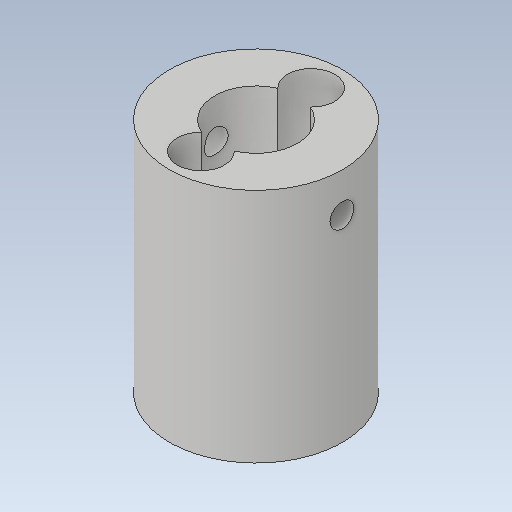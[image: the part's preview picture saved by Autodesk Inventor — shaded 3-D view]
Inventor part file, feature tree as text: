
AUTODESK INVENTOR PART (.ipt)
format: ipt  version: 2020.1 (Build 241239000, 239)  size: 161,792 bytes
history: native  units: mm
features: extrude x5, sketch x5, other x2
ambient origin geometry x8: Origin, YZ Plane, XZ Plane, XY Plane, X Axis, Y Axis, Z Axis, Center Point
bodies: Body1 (feature_tree)
feature tree (12):
  extrude  "Extrusión6"  Depth=7.0mm
  extrude  "Extrusión7"  Depth=3.0mm
  extrude  "Extrusión8"  Depth=3.0mm TaperAngle=0.0deg
  extrude  "Extrusión10"  Depth=6.0mm
  other  "Edición directa2"
  extrude  "Extrusión11"  Depth=12.0mm
  sketch  "Boceto5"  dims[d25=22.0mm d26=7.0mm]
  sketch  "Boceto6"  dims[d27=7.0mm d28=3.0mm]
  sketch  "Boceto7"  dims[d29=3.0mm d30=4.0mm d31=0.0mm]
  sketch  "Boceto8"  dims[d32=6.0mm d33=6.0mm]
  sketch  "Boceto9"  dims[d34=8.0mm d35=0.0mm d36=10.5mm d37=20.0mm d38=0.0mm d39=23.0mm d43=2.0mm d44=3.0mm d45=22.0mm d46=0.0mm d47=0.0mm d48=0.0mm d49=-2.0mm d52=6.0mm d53=12.0mm d54=0.0mm]
  other  "Desplazar2"
